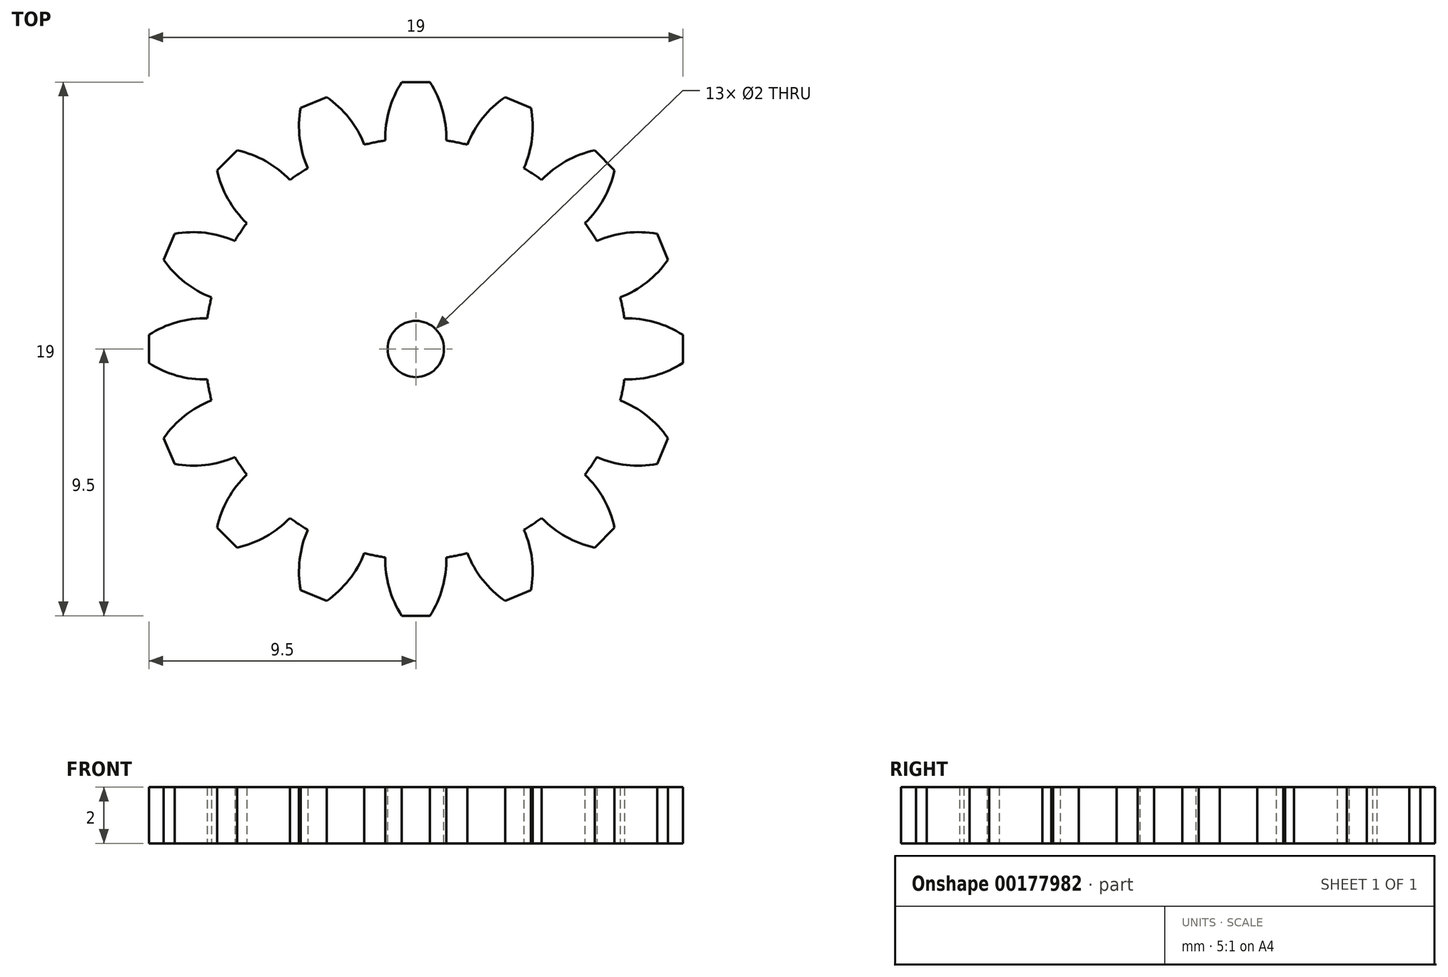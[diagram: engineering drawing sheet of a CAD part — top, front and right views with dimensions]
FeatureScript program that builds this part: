
annotation { "Feature Type Name" : "Feature", "Feature Type Description" : "" }
export const myFeature = defineFeature(function(context is Context, id is Id, definition is map)
    precondition{}
    {
        {
            var Q0;
            Q0=qCreatedBy(makeId("Top.planeOp"),FACE);
            var sketch = newSketch(context, id + "F0", { "sketchPlane" : qUnion([Q0])});
            skCircle(sketch, "E0", {"center": v(0, 0) * mm, "radius": 7.5 * mm});
            skLineSegment(sketch, "E1", {"start": v(0, 0) * mm, "end": v(0, 7.5) * mm, "construction": true});
            skArc(sketch, "E2", {"start": v(-0.5, 9.5) * mm, "mid": v(-0.95, 8.5) * mm, "end": v(-1.09, 7.42) * mm});
            skLineSegment(sketch, "E3", {"start": v(0, 9.5) * mm, "end": v(-0.5, 9.5) * mm});
            skLineSegment(sketch, "E4.MirrorCS", {"start": v(0, 9.5) * mm, "end": v(0.5, 9.5) * mm});
            skArc(sketch, "E5.MirrorCS", {"start": v(0.5, 9.5) * mm, "mid": v(0.95, 8.5) * mm, "end": v(1.09, 7.42) * mm});
            skArc(sketch, "E6.1.0", {"start": v(-3.17, 8.97) * mm, "mid": v(-2.38, 8.22) * mm, "end": v(-1.83, 7.27) * mm});
            skLineSegment(sketch, "E6.1.1", {"start": v(-3.64, 8.78) * mm, "end": v(-3.17, 8.97) * mm});
            skLineSegment(sketch, "E6.1.2", {"start": v(-3.64, 8.78) * mm, "end": v(-4.1, 8.59) * mm});
            skArc(sketch, "E6.1.3", {"start": v(-4.1, 8.59) * mm, "mid": v(-4.13, 7.5) * mm, "end": v(-3.85, 6.44) * mm});
            skArc(sketch, "E6.2.0", {"start": v(-6.36, 7.07) * mm, "mid": v(-5.34, 6.69) * mm, "end": v(-4.48, 6.02) * mm});
            skLineSegment(sketch, "E6.2.1", {"start": v(-6.72, 6.72) * mm, "end": v(-6.36, 7.07) * mm});
            skLineSegment(sketch, "E6.2.2", {"start": v(-6.72, 6.72) * mm, "end": v(-7.07, 6.36) * mm});
            skArc(sketch, "E6.2.3", {"start": v(-7.07, 6.36) * mm, "mid": v(-6.69, 5.34) * mm, "end": v(-6.02, 4.48) * mm});
            skArc(sketch, "E6.3.0", {"start": v(-8.59, 4.1) * mm, "mid": v(-7.5, 4.13) * mm, "end": v(-6.44, 3.85) * mm});
            skLineSegment(sketch, "E6.3.1", {"start": v(-8.78, 3.64) * mm, "end": v(-8.59, 4.1) * mm});
            skLineSegment(sketch, "E6.3.2", {"start": v(-8.78, 3.64) * mm, "end": v(-8.97, 3.17) * mm});
            skArc(sketch, "E6.3.3", {"start": v(-8.97, 3.17) * mm, "mid": v(-8.22, 2.38) * mm, "end": v(-7.27, 1.83) * mm});
            skArc(sketch, "E6.4.0", {"start": v(-9.5, 0.5) * mm, "mid": v(-8.5, 0.95) * mm, "end": v(-7.42, 1.09) * mm});
            skLineSegment(sketch, "E6.4.1", {"start": v(-9.5, 0) * mm, "end": v(-9.5, 0.5) * mm});
            skLineSegment(sketch, "E6.4.2", {"start": v(-9.5, 0) * mm, "end": v(-9.5, -0.5) * mm});
            skArc(sketch, "E6.4.3", {"start": v(-9.5, -0.5) * mm, "mid": v(-8.5, -0.95) * mm, "end": v(-7.42, -1.09) * mm});
            skArc(sketch, "E6.5.0", {"start": v(-8.97, -3.17) * mm, "mid": v(-8.22, -2.38) * mm, "end": v(-7.27, -1.83) * mm});
            skLineSegment(sketch, "E6.5.1", {"start": v(-8.78, -3.64) * mm, "end": v(-8.97, -3.17) * mm});
            skLineSegment(sketch, "E6.5.2", {"start": v(-8.78, -3.64) * mm, "end": v(-8.59, -4.1) * mm});
            skArc(sketch, "E6.5.3", {"start": v(-8.59, -4.1) * mm, "mid": v(-7.5, -4.13) * mm, "end": v(-6.44, -3.85) * mm});
            skArc(sketch, "E6.6.0", {"start": v(-7.07, -6.36) * mm, "mid": v(-6.69, -5.34) * mm, "end": v(-6.02, -4.48) * mm});
            skLineSegment(sketch, "E6.6.1", {"start": v(-6.72, -6.72) * mm, "end": v(-7.07, -6.36) * mm});
            skLineSegment(sketch, "E6.6.2", {"start": v(-6.72, -6.72) * mm, "end": v(-6.36, -7.07) * mm});
            skArc(sketch, "E6.6.3", {"start": v(-6.36, -7.07) * mm, "mid": v(-5.34, -6.69) * mm, "end": v(-4.48, -6.02) * mm});
            skArc(sketch, "E6.7.0", {"start": v(-4.1, -8.59) * mm, "mid": v(-4.13, -7.5) * mm, "end": v(-3.85, -6.44) * mm});
            skLineSegment(sketch, "E6.7.1", {"start": v(-3.64, -8.78) * mm, "end": v(-4.1, -8.59) * mm});
            skLineSegment(sketch, "E6.7.2", {"start": v(-3.64, -8.78) * mm, "end": v(-3.17, -8.97) * mm});
            skArc(sketch, "E6.7.3", {"start": v(-3.17, -8.97) * mm, "mid": v(-2.38, -8.22) * mm, "end": v(-1.83, -7.27) * mm});
            skArc(sketch, "E6.8.0", {"start": v(-0.5, -9.5) * mm, "mid": v(-0.95, -8.5) * mm, "end": v(-1.09, -7.42) * mm});
            skLineSegment(sketch, "E6.8.1", {"start": v(0, -9.5) * mm, "end": v(-0.5, -9.5) * mm});
            skLineSegment(sketch, "E6.8.2", {"start": v(0, -9.5) * mm, "end": v(0.5, -9.5) * mm});
            skArc(sketch, "E6.8.3", {"start": v(0.5, -9.5) * mm, "mid": v(0.95, -8.5) * mm, "end": v(1.09, -7.42) * mm});
            skArc(sketch, "E6.9.0", {"start": v(3.17, -8.97) * mm, "mid": v(2.38, -8.22) * mm, "end": v(1.83, -7.27) * mm});
            skLineSegment(sketch, "E6.9.1", {"start": v(3.64, -8.78) * mm, "end": v(3.17, -8.97) * mm});
            skLineSegment(sketch, "E6.9.2", {"start": v(3.64, -8.78) * mm, "end": v(4.1, -8.59) * mm});
            skArc(sketch, "E6.9.3", {"start": v(4.1, -8.59) * mm, "mid": v(4.13, -7.5) * mm, "end": v(3.85, -6.44) * mm});
            skArc(sketch, "E6.10.0", {"start": v(6.36, -7.07) * mm, "mid": v(5.34, -6.69) * mm, "end": v(4.48, -6.02) * mm});
            skLineSegment(sketch, "E6.10.1", {"start": v(6.72, -6.72) * mm, "end": v(6.36, -7.07) * mm});
            skLineSegment(sketch, "E6.10.2", {"start": v(6.72, -6.72) * mm, "end": v(7.07, -6.36) * mm});
            skArc(sketch, "E6.10.3", {"start": v(7.07, -6.36) * mm, "mid": v(6.69, -5.34) * mm, "end": v(6.02, -4.48) * mm});
            skArc(sketch, "E6.11.0", {"start": v(8.59, -4.1) * mm, "mid": v(7.5, -4.13) * mm, "end": v(6.44, -3.85) * mm});
            skLineSegment(sketch, "E6.11.1", {"start": v(8.78, -3.64) * mm, "end": v(8.59, -4.1) * mm});
            skLineSegment(sketch, "E6.11.2", {"start": v(8.78, -3.64) * mm, "end": v(8.97, -3.17) * mm});
            skArc(sketch, "E6.11.3", {"start": v(8.97, -3.17) * mm, "mid": v(8.22, -2.38) * mm, "end": v(7.27, -1.83) * mm});
            skArc(sketch, "E6.12.0", {"start": v(9.5, -0.5) * mm, "mid": v(8.5, -0.95) * mm, "end": v(7.42, -1.09) * mm});
            skLineSegment(sketch, "E6.12.1", {"start": v(9.5, 0) * mm, "end": v(9.5, -0.5) * mm});
            skLineSegment(sketch, "E6.12.2", {"start": v(9.5, 0) * mm, "end": v(9.5, 0.5) * mm});
            skArc(sketch, "E6.12.3", {"start": v(9.5, 0.5) * mm, "mid": v(8.5, 0.95) * mm, "end": v(7.42, 1.09) * mm});
            skArc(sketch, "E6.13.0", {"start": v(8.97, 3.17) * mm, "mid": v(8.22, 2.38) * mm, "end": v(7.27, 1.83) * mm});
            skLineSegment(sketch, "E6.13.1", {"start": v(8.78, 3.64) * mm, "end": v(8.97, 3.17) * mm});
            skLineSegment(sketch, "E6.13.2", {"start": v(8.78, 3.64) * mm, "end": v(8.59, 4.1) * mm});
            skArc(sketch, "E6.13.3", {"start": v(8.59, 4.1) * mm, "mid": v(7.5, 4.13) * mm, "end": v(6.44, 3.85) * mm});
            skArc(sketch, "E6.14.0", {"start": v(7.07, 6.36) * mm, "mid": v(6.69, 5.34) * mm, "end": v(6.02, 4.48) * mm});
            skLineSegment(sketch, "E6.14.1", {"start": v(6.72, 6.72) * mm, "end": v(7.07, 6.36) * mm});
            skLineSegment(sketch, "E6.14.2", {"start": v(6.72, 6.72) * mm, "end": v(6.36, 7.07) * mm});
            skArc(sketch, "E6.14.3", {"start": v(6.36, 7.07) * mm, "mid": v(5.34, 6.69) * mm, "end": v(4.48, 6.02) * mm});
            skArc(sketch, "E6.15.0", {"start": v(4.1, 8.59) * mm, "mid": v(4.13, 7.5) * mm, "end": v(3.85, 6.44) * mm});
            skLineSegment(sketch, "E6.15.1", {"start": v(3.64, 8.78) * mm, "end": v(4.1, 8.59) * mm});
            skLineSegment(sketch, "E6.15.2", {"start": v(3.64, 8.78) * mm, "end": v(3.17, 8.97) * mm});
            skArc(sketch, "E6.15.3", {"start": v(3.17, 8.97) * mm, "mid": v(2.38, 8.22) * mm, "end": v(1.83, 7.27) * mm});
            skSolve(sketch);
        }
        {
            var Q0;
            Q0 = qSketchRegion(id + "F0", true);
            extrude(context, id + "F1", {"entities" : qUnion([Q0]), "depth" : 2 * mm});
        }
        {
            var Q0;
            Q0=makeQuery(id+"F1.opExtrude","CAP_FACE",FACE,{"disambiguationData":[OSD([sQuery(id+"F0.wireOp",EDGE,"E0"),sQuery(id+"F0.wireOp",EDGE,"E2"),sQuery(id+"F0.wireOp",EDGE,"E3"),sQuery(id+"F0.wireOp",EDGE,"E4.MirrorCS"),sQuery(id+"F0.wireOp",EDGE,"E5.MirrorCS"),sQuery(id+"F0.wireOp",EDGE,"E6.1.0"),sQuery(id+"F0.wireOp",EDGE,"E6.1.1"),sQuery(id+"F0.wireOp",EDGE,"E6.1.2"),sQuery(id+"F0.wireOp",EDGE,"E6.1.3"),sQuery(id+"F0.wireOp",EDGE,"E6.2.0"),sQuery(id+"F0.wireOp",EDGE,"E6.2.1"),sQuery(id+"F0.wireOp",EDGE,"E6.2.2"),sQuery(id+"F0.wireOp",EDGE,"E6.2.3"),sQuery(id+"F0.wireOp",EDGE,"E6.3.0"),sQuery(id+"F0.wireOp",EDGE,"E6.3.1"),sQuery(id+"F0.wireOp",EDGE,"E6.3.2"),sQuery(id+"F0.wireOp",EDGE,"E6.3.3"),sQuery(id+"F0.wireOp",EDGE,"E6.4.0"),sQuery(id+"F0.wireOp",EDGE,"E6.4.1"),sQuery(id+"F0.wireOp",EDGE,"E6.4.2"),sQuery(id+"F0.wireOp",EDGE,"E6.4.3"),sQuery(id+"F0.wireOp",EDGE,"E6.5.0"),sQuery(id+"F0.wireOp",EDGE,"E6.5.1"),sQuery(id+"F0.wireOp",EDGE,"E6.5.2"),sQuery(id+"F0.wireOp",EDGE,"E6.5.3"),sQuery(id+"F0.wireOp",EDGE,"E6.6.0"),sQuery(id+"F0.wireOp",EDGE,"E6.6.1"),sQuery(id+"F0.wireOp",EDGE,"E6.6.2"),sQuery(id+"F0.wireOp",EDGE,"E6.6.3"),sQuery(id+"F0.wireOp",EDGE,"E6.7.0"),sQuery(id+"F0.wireOp",EDGE,"E6.7.1"),sQuery(id+"F0.wireOp",EDGE,"E6.7.2"),sQuery(id+"F0.wireOp",EDGE,"E6.7.3"),sQuery(id+"F0.wireOp",EDGE,"E6.8.0"),sQuery(id+"F0.wireOp",EDGE,"E6.8.1"),sQuery(id+"F0.wireOp",EDGE,"E6.8.2"),sQuery(id+"F0.wireOp",EDGE,"E6.8.3"),sQuery(id+"F0.wireOp",EDGE,"E6.9.0"),sQuery(id+"F0.wireOp",EDGE,"E6.9.1"),sQuery(id+"F0.wireOp",EDGE,"E6.9.2"),sQuery(id+"F0.wireOp",EDGE,"E6.9.3"),sQuery(id+"F0.wireOp",EDGE,"E6.10.0"),sQuery(id+"F0.wireOp",EDGE,"E6.10.1"),sQuery(id+"F0.wireOp",EDGE,"E6.10.2"),sQuery(id+"F0.wireOp",EDGE,"E6.10.3"),sQuery(id+"F0.wireOp",EDGE,"E6.11.0"),sQuery(id+"F0.wireOp",EDGE,"E6.11.1"),sQuery(id+"F0.wireOp",EDGE,"E6.11.2"),sQuery(id+"F0.wireOp",EDGE,"E6.11.3"),sQuery(id+"F0.wireOp",EDGE,"E6.12.0"),sQuery(id+"F0.wireOp",EDGE,"E6.12.1"),sQuery(id+"F0.wireOp",EDGE,"E6.12.2"),sQuery(id+"F0.wireOp",EDGE,"E6.12.3"),sQuery(id+"F0.wireOp",EDGE,"E6.13.0"),sQuery(id+"F0.wireOp",EDGE,"E6.13.1"),sQuery(id+"F0.wireOp",EDGE,"E6.13.2"),sQuery(id+"F0.wireOp",EDGE,"E6.13.3"),sQuery(id+"F0.wireOp",EDGE,"E6.14.0"),sQuery(id+"F0.wireOp",EDGE,"E6.14.1"),sQuery(id+"F0.wireOp",EDGE,"E6.14.2"),sQuery(id+"F0.wireOp",EDGE,"E6.14.3"),sQuery(id+"F0.wireOp",EDGE,"E6.15.0"),sQuery(id+"F0.wireOp",EDGE,"E6.15.1"),sQuery(id+"F0.wireOp",EDGE,"E6.15.2"),sQuery(id+"F0.wireOp",EDGE,"E6.15.3")])],"isStart":false});
            var sketch = newSketch(context, id + "F2", { "sketchPlane" : qUnion([Q0])});
            skCircle(sketch, "E7", {"center": v(0, 0) * mm, "radius": 1 * mm});
            skSolve(sketch);
        }
        {
            var Q0;
            Q0 = qSketchRegion(id + "F2", true);
            extrude(context, id + "F3", {"entities" : qUnion([Q0]), "operationType" : NewBodyOperationType.REMOVE, "oppositeDirection" : true, "depth" : 25 * mm});
        }
    });
